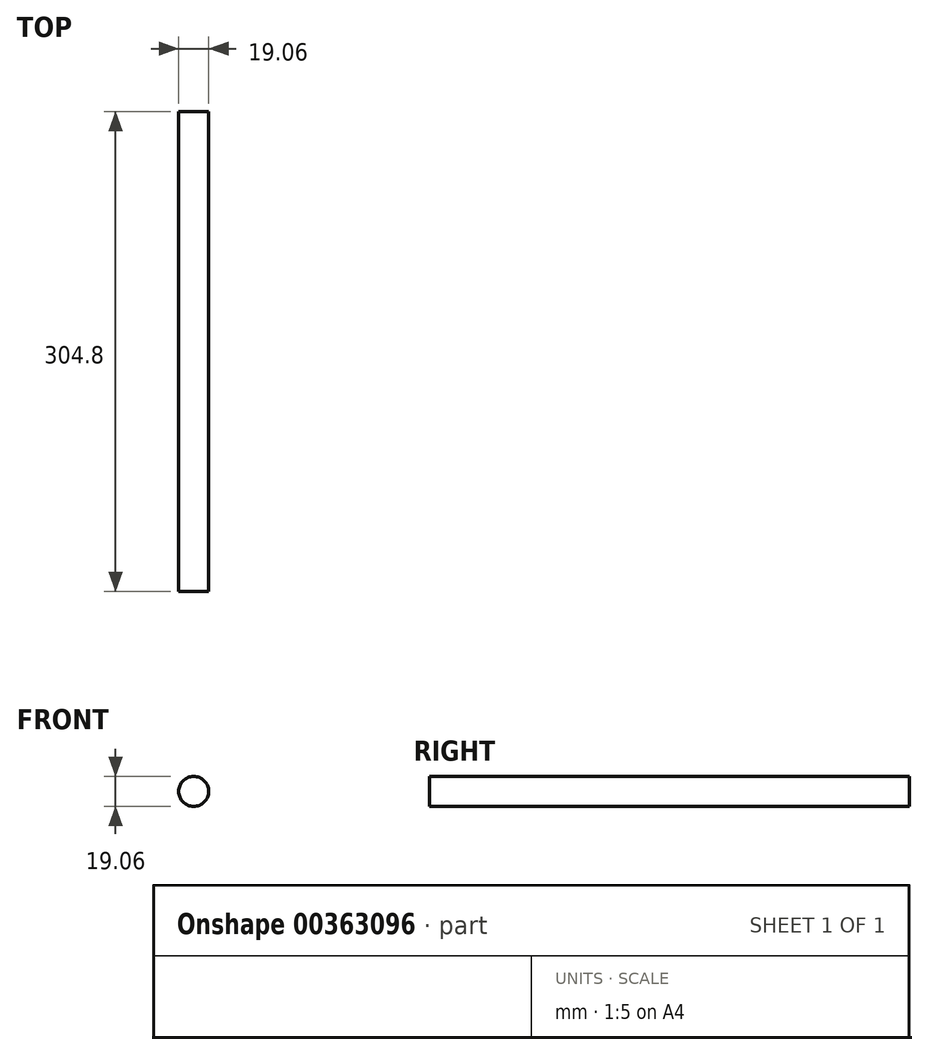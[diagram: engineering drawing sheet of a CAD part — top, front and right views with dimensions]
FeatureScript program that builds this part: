
annotation { "Feature Type Name" : "Feature", "Feature Type Description" : "" }
export const myFeature = defineFeature(function(context is Context, id is Id, definition is map)
    precondition{}
    {
        {
            var Q0;
            Q0=qCreatedBy(makeId("Front.planeOp"),FACE);
            var sketch = newSketch(context, id + "F0", { "sketchPlane" : qUnion([Q0])});
            skCircle(sketch, "E0", {"center": v(0, 0) * mm, "radius": 9.53 * mm});
            skSolve(sketch);
        }
        {
            var Q0;
            Q0 = qSketchRegion(id + "F0", true);
            extrude(context, id + "F1", {"entities" : qUnion([Q0]), "depth" : 304.8 * mm});
        }
    });
